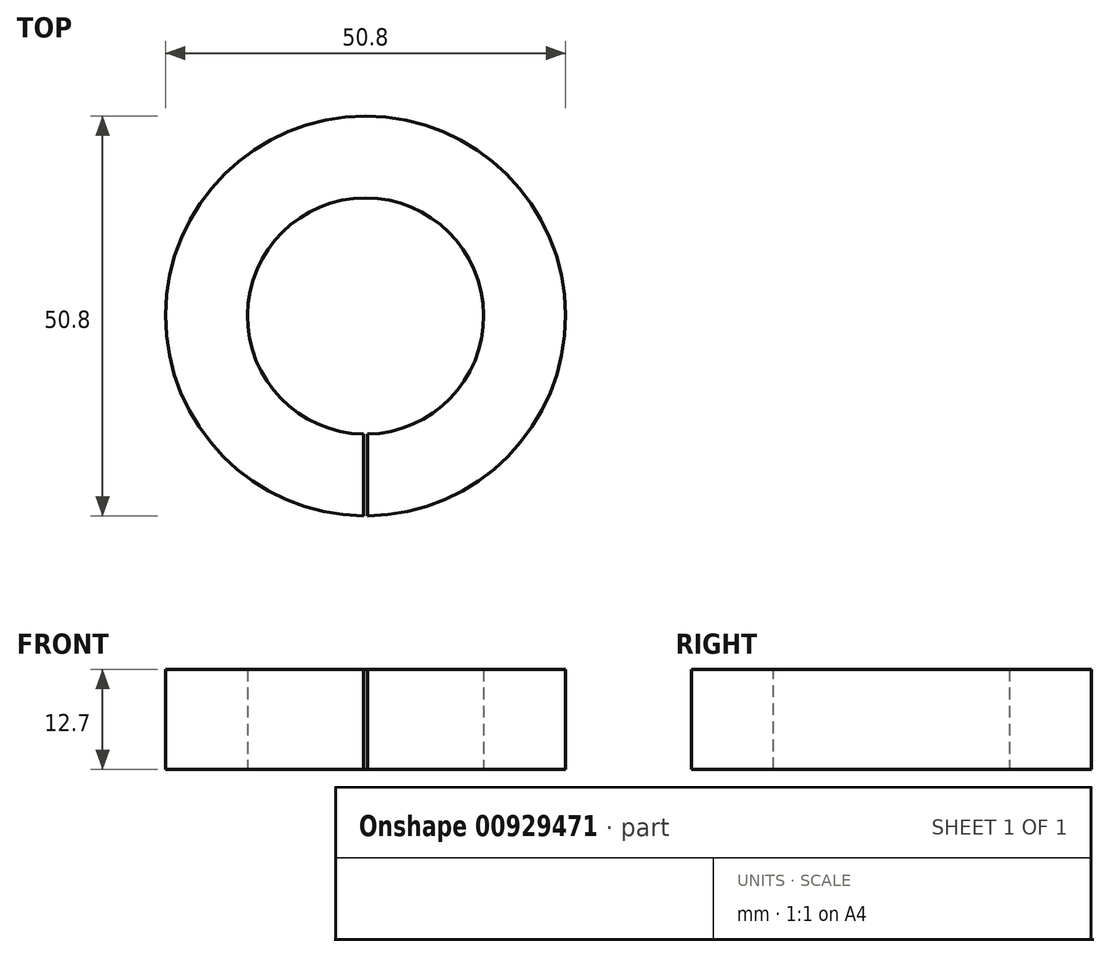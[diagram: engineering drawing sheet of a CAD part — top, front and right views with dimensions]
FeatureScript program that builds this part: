
annotation { "Feature Type Name" : "Feature", "Feature Type Description" : "" }
export const myFeature = defineFeature(function(context is Context, id is Id, definition is map)
    precondition{}
    {
        {
            var Q0;
            Q0=qCreatedBy(makeId("Top.planeOp"),FACE);
            var sketch = newSketch(context, id + "F0", { "sketchPlane" : qUnion([Q0])});
            skCircle(sketch, "E0", {"center": v(0, 0) * mm, "radius": 15 * mm});
            skCircle(sketch, "E1", {"center": v(0, 0) * mm, "radius": 25.4 * mm});
            skSolve(sketch);
        }
        {
            var Q0;
            Q0 = qSketchRegion(id + "F0", true);
            extrude(context, id + "F1", {"entities" : qUnion([Q0]), "endBound" : BoundingType.SYMMETRIC, "depth" : 12.7 * mm, "offsetDistance" : 25.4 * mm});
        }
        {
            var Q0;
            Q0=makeQuery(id+"F1.opExtrude","CAP_FACE",FACE,{"disambiguationData":[OSD([sQuery(id+"F0.wireOp",EDGE,"E0"),sQuery(id+"F0.wireOp",EDGE,"E1")])],"isStart":false});
            var sketch = newSketch(context, id + "F2", { "sketchPlane" : qUnion([Q0])});
            skLineSegment(sketch, "E2", {"start": v(0, 0) * mm, "end": v(0, -25.4) * mm, "construction": true});
            skLineSegment(sketch, "E3.0", {"start": v(-0.25, -15) * mm, "end": v(-0.25, -25.4) * mm});
            skLineSegment(sketch, "E4.MirrorCS", {"start": v(0.25, -15) * mm, "end": v(0.25, -25.4) * mm});
            skArc(sketch, "E5.0", {"start": v(-0.25, -15) * mm, "mid": v(0, -15) * mm, "end": v(0.25, -15) * mm});
            skArc(sketch, "E6.0", {"start": v(-0.25, -25.4) * mm, "mid": v(0, -25.4) * mm, "end": v(0.25, -25.4) * mm});
            skPoint(sketch, "E7.orphan", {"position": v(-0.25, 0) * mm});
            skPoint(sketch, "E8.orphan", {"position": v(0.25, 0) * mm});
            skSolve(sketch);
        }
        {
            var Q0;
            Q0 = qSketchRegion(id + "F2", true);
            extrude(context, id + "F3", {"entities" : qUnion([Q0]), "operationType" : NewBodyOperationType.REMOVE, "endBound" : BoundingType.THROUGH_ALL, "oppositeDirection" : true, "depth" : 25.4 * mm, "offsetDistance" : 25.4 * mm});
        }
    });
